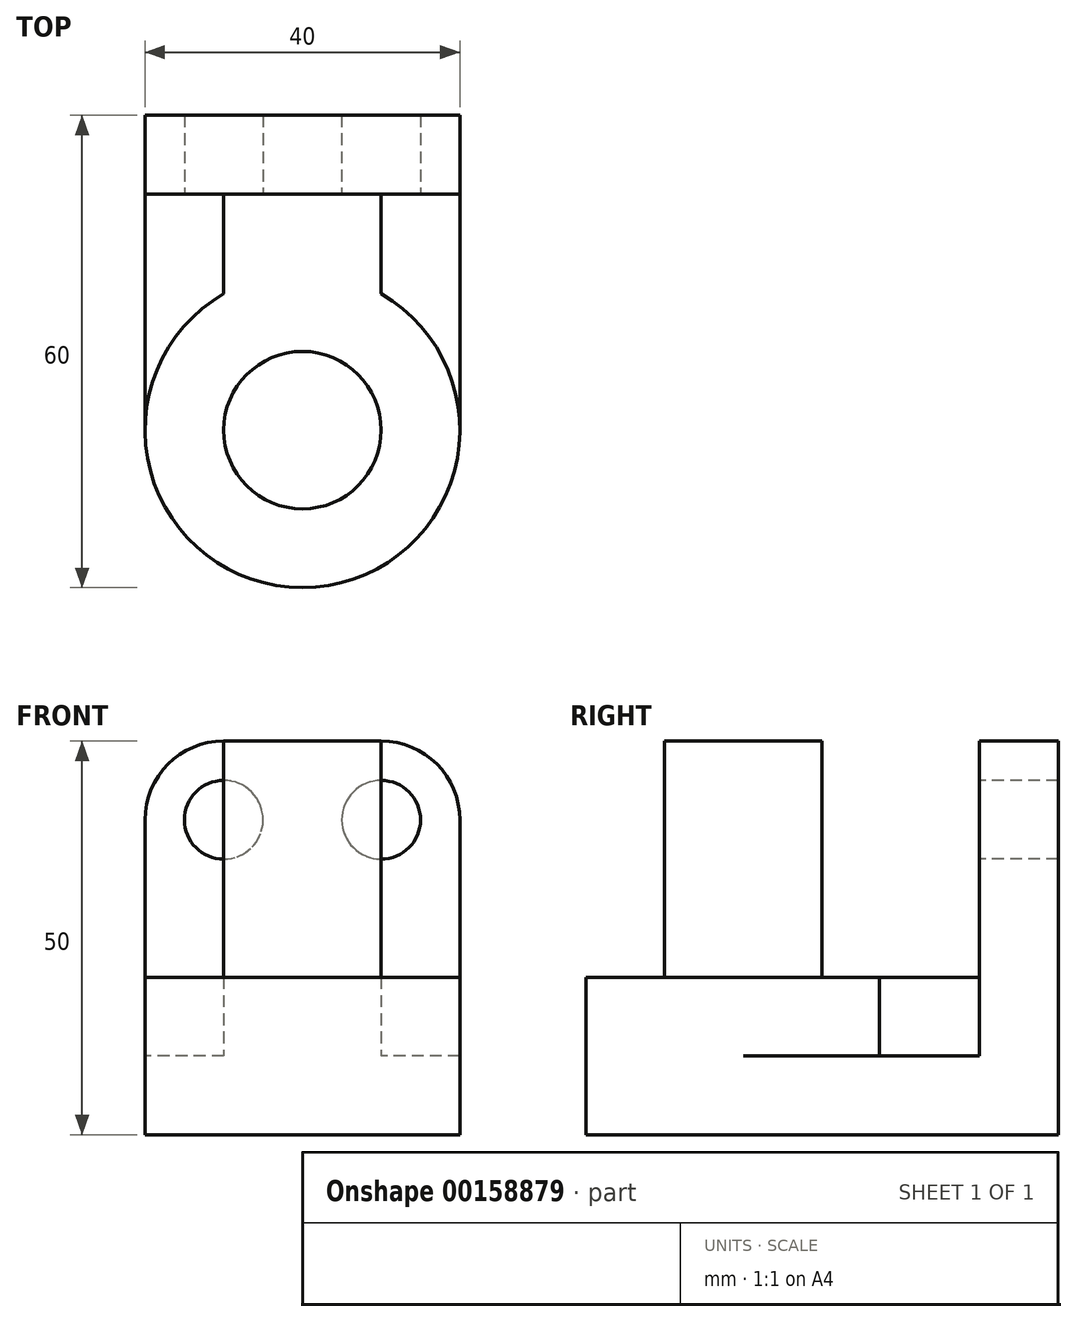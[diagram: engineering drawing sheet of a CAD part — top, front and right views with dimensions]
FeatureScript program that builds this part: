
annotation { "Feature Type Name" : "Feature", "Feature Type Description" : "" }
export const myFeature = defineFeature(function(context is Context, id is Id, definition is map)
    precondition{}
    {
        {
            var Q0;
            Q0=qCreatedBy(makeId("Right.planeOp"),FACE);
            var sketch = newSketch(context, id + "F0", { "sketchPlane" : qUnion([Q0])});
            skLineSegment(sketch, "E0", {"start": v(0, 0) * mm, "end": v(0, 50) * mm});
            skLineSegment(sketch, "E1", {"start": v(0, 50) * mm, "end": v(-10, 50) * mm});
            skLineSegment(sketch, "E2", {"start": v(-10, 50) * mm, "end": v(-10, 10) * mm});
            skLineSegment(sketch, "E3", {"start": v(-10, 10) * mm, "end": v(-60, 10) * mm});
            skLineSegment(sketch, "E4", {"start": v(-60, 10) * mm, "end": v(-60, 0) * mm});
            skLineSegment(sketch, "E5", {"start": v(-60, 0) * mm, "end": v(0, 0) * mm});
            skSolve(sketch);
        }
        {
            var Q0;
            Q0=makeQuery(id+"F0.imprint","IMPRINT",FACE,{"disambiguationData":[TD([[makeQuery(id+"F0.imprint","IMPRINT",EDGE,{"derivedFrom":sQuery(id+"F0.wireOp",EDGE,"E0")}),1.0]])]});
            extrude(context, id + "F1", {"entities" : qUnion([Q0]), "endBound" : BoundingType.SYMMETRIC, "depth" : 40 * mm});
        }
        {
            var Q0;
            Q0=makeQuery(id+"F1.opExtrude","CAP_EDGE",EDGE,{"disambiguationData":[OSD([sQuery(id+"F0.wireOp",EDGE,"E4")])],"isStart":true});
            var Q1;
            Q1=makeQuery(id+"F1.opExtrude","CAP_EDGE",EDGE,{"disambiguationData":[OSD([sQuery(id+"F0.wireOp",EDGE,"E4")])],"isStart":false});
            fillet(context, id + "F2", {"entities" : qUnion([Q0, Q1]), "radius" : 20 * mm, "tangentPropagation" : true, "allowEdgeOverflow" : false});
        }
        {
            var Q0;
            Q0=makeQuery(id+"F1.opExtrude","CAP_EDGE",EDGE,{"disambiguationData":[OSD([sQuery(id+"F0.wireOp",EDGE,"E1")])],"isStart":true});
            var Q1;
            Q1=makeQuery(id+"F1.opExtrude","CAP_EDGE",EDGE,{"disambiguationData":[OSD([sQuery(id+"F0.wireOp",EDGE,"E1")])],"isStart":false});
            fillet(context, id + "F3", {"entities" : qUnion([Q0, Q1]), "radius" : 10 * mm, "tangentPropagation" : true, "allowEdgeOverflow" : false});
        }
        {
            var Q0;
            Q0=makeQuery(id+"F1.opExtrude","SWEPT_FACE",FACE,{"disambiguationData":[OSD([sQuery(id+"F0.wireOp",EDGE,"E3")])]});
            var sketch = newSketch(context, id + "F4", { "sketchPlane" : qUnion([Q0])});
            skArc(sketch, "E6", {"start": v(-10, -22.68) * mm, "mid": v(0, -60) * mm, "end": v(10, -22.68) * mm});
            skLineSegment(sketch, "E7.bottom", {"start": v(-10, -10) * mm, "end": v(10, -10) * mm});
            skLineSegment(sketch, "E7.left", {"start": v(-10, -10) * mm, "end": v(-10, -22.68) * mm});
            skLineSegment(sketch, "E7.right", {"start": v(10, -10) * mm, "end": v(10, -22.68) * mm});
            skSolve(sketch);
        }
        {
            var Q0;
            {var subQ0=sQuery(id+"F4.wireOp",EDGE,"E6");var subQ1=sQuery(id+"F0.wireOp",EDGE,"E3");var subQ2=makeQuery(id+"F4.imprint","INTERSECT",VERTEX,{"derivedFrom":[makeQuery(id+"F1.opExtrude","CAP_EDGE",EDGE,{"disambiguationData":[OSD([subQ1])],"isStart":true}),subQ0]});Q0=makeQuery(id+"F4.imprint","IMPRINT",FACE,{"disambiguationData":[TD([[makeQuery(id+"F4.imprint","IMPRINT",EDGE,{"disambiguationData":[TD([[subQ2,1.0]])],"derivedFrom":subQ0}),1.0]])]});}
            extrude(context, id + "F5", {"entities" : qUnion([Q0]), "operationType" : NewBodyOperationType.ADD, "depth" : 10 * mm});
        }
        {
            var Q0;
            Q0=makeQuery(id+"F5.opExtrude","CAP_FACE",FACE,{"disambiguationData":[OSD([sQuery(id+"F4.wireOp",EDGE,"E6")])],"isStart":false});
            var sketch = newSketch(context, id + "F6", { "sketchPlane" : qUnion([Q0])});
            skCircle(sketch, "E8", {"center": v(0, -40) * mm, "radius": 10 * mm});
            skSolve(sketch);
        }
        {
            var Q0;
            Q0=makeQuery(id+"F6.imprint","IMPRINT",FACE,{"disambiguationData":[TD([[makeQuery(id+"F6.imprint","IMPRINT",EDGE,{"derivedFrom":sQuery(id+"F6.wireOp",EDGE,"E8")}),1.0]])]});
            extrude(context, id + "F7", {"entities" : qUnion([Q0]), "operationType" : NewBodyOperationType.ADD, "depth" : 30 * mm});
        }
        {
            var Q0;
            Q0=makeQuery(id+"F1.opExtrude","SWEPT_FACE",FACE,{"disambiguationData":[OSD([sQuery(id+"F0.wireOp",EDGE,"E2")])]});
            var sketch = newSketch(context, id + "F8", { "sketchPlane" : qUnion([Q0])});
            skPoint(sketch, "E9", {"position": v(50.95, 23.91) * mm});
            skPoint(sketch, "E10", {"position": v(-10, 40) * mm});
            skPoint(sketch, "E11", {"position": v(10, 40) * mm});
            skSolve(sketch);
        }
        {
            var Q0;
            Q0=sQuery(id+"F8.wireOp",VERTEX,"E11");
            var Q1;
            Q1=sQuery(id+"F8.wireOp",VERTEX,"E10");
            var Q2;
            Q2=makeQuery(id+"F1.opExtrude","SWEPT_BODY",BODY,{"disambiguationData":[OSD([sQuery(id+"F0.wireOp",EDGE,"E0"),sQuery(id+"F0.wireOp",EDGE,"E1"),sQuery(id+"F0.wireOp",EDGE,"E2"),sQuery(id+"F0.wireOp",EDGE,"E3"),sQuery(id+"F0.wireOp",EDGE,"E4"),sQuery(id+"F0.wireOp",EDGE,"E5")])]});
            hole(context, id + "F9", {"style" : HoleStyle.SIMPLE, "endStyle" : HoleEndStyle.THROUGH, "holeDiameter" : 10 * mm, "locations" : qUnion([Q0, Q1]), "scope" : qUnion([Q2]), "isTappedThrough" : true});
        }
    });
